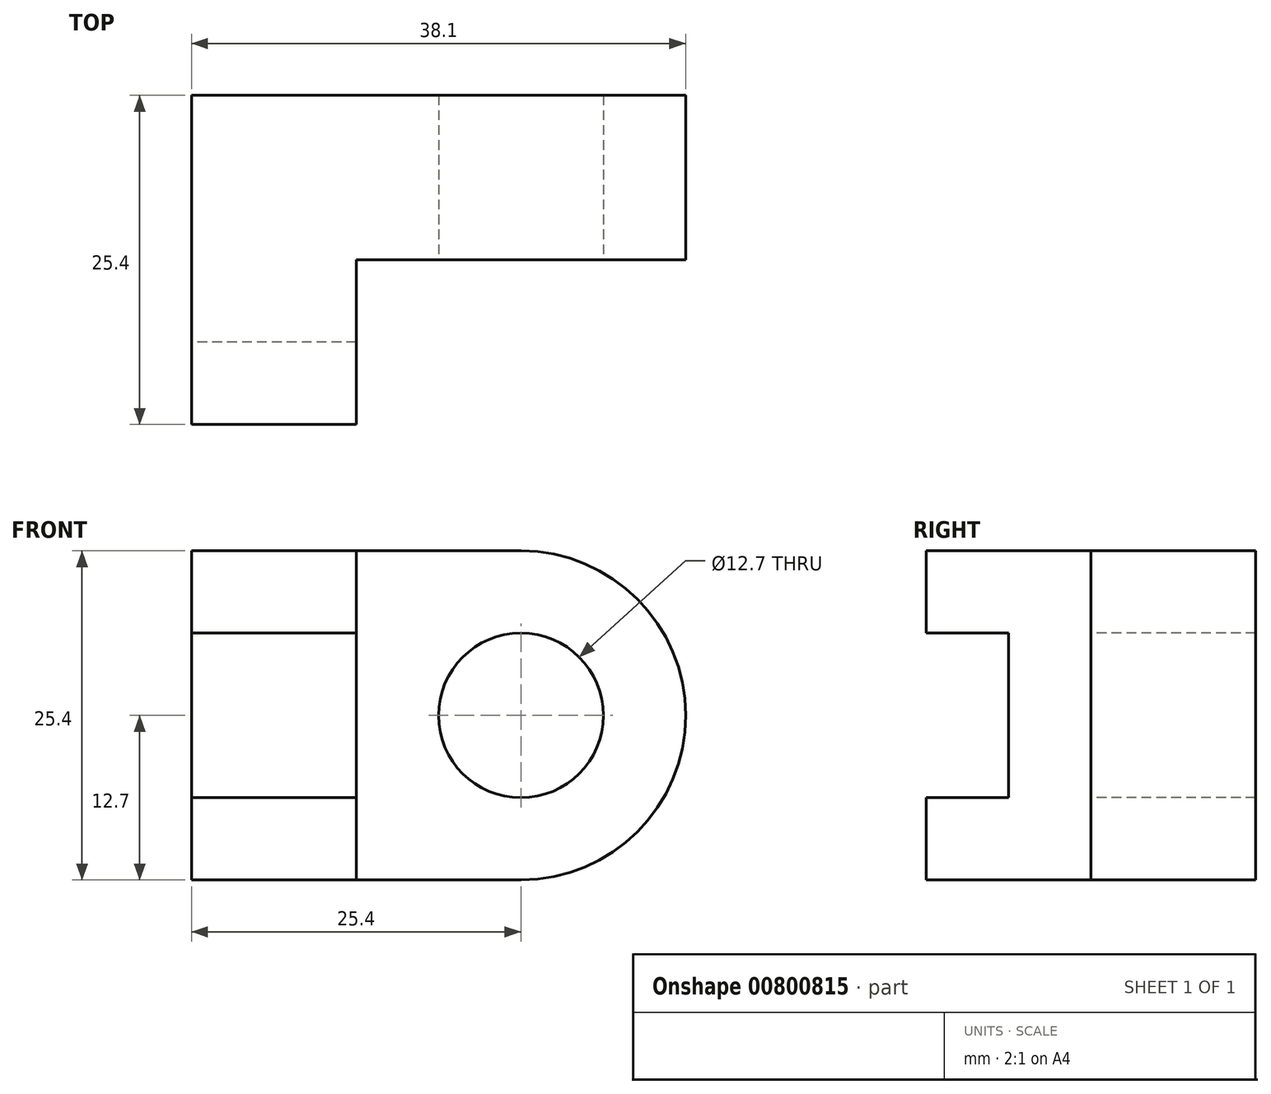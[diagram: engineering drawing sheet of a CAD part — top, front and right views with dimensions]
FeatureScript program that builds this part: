
annotation { "Feature Type Name" : "Feature", "Feature Type Description" : "" }
export const myFeature = defineFeature(function(context is Context, id is Id, definition is map)
    precondition{}
    {
        {
            var Q0;
            Q0=qCreatedBy(makeId("Front.planeOp"),FACE);
            var sketch = newSketch(context, id + "F0", { "sketchPlane" : qUnion([Q0])});
            skLineSegment(sketch, "E0", {"start": v(0, 0) * mm, "end": v(38.1, 0) * mm});
            skLineSegment(sketch, "E1", {"start": v(38.1, 0) * mm, "end": v(38.1, 25.4) * mm});
            skLineSegment(sketch, "E2", {"start": v(38.1, 25.4) * mm, "end": v(0, 25.4) * mm});
            skLineSegment(sketch, "E3", {"start": v(0, 25.4) * mm, "end": v(0, 0) * mm});
            skSolve(sketch);
        }
        {
            var Q0;
            Q0=makeQuery(id+"F0.imprint","IMPRINT",FACE,{"disambiguationData":[TD([[makeQuery(id+"F0.imprint","IMPRINT",EDGE,{"derivedFrom":sQuery(id+"F0.wireOp",EDGE,"E0")}),1.0]])]});
            extrude(context, id + "F1", {"entities" : qUnion([Q0]), "depth" : 25.4 * mm, "offsetDistance" : 25.4 * mm});
        }
        {
            var Q0;
            Q0=makeQuery(id+"F1.opExtrude","CAP_FACE",FACE,{"disambiguationData":[OSD([sQuery(id+"F0.wireOp",EDGE,"E0"),sQuery(id+"F0.wireOp",EDGE,"E1"),sQuery(id+"F0.wireOp",EDGE,"E2"),sQuery(id+"F0.wireOp",EDGE,"E3")])],"isStart":false});
            var sketch = newSketch(context, id + "F2", { "sketchPlane" : qUnion([Q0])});
            skLineSegment(sketch, "E4", {"start": v(0, 25.4) * mm, "end": v(12.7, 25.4) * mm, "construction": true});
            skLineSegment(sketch, "E5", {"start": v(12.7, 25.4) * mm, "end": v(12.7, 0) * mm});
            skSolve(sketch);
        }
        {
            var Q0;
            Q0 = qSketchRegion(id + "F2", true);
            var Q1;
            {var subQ0=sQuery(id+"F2.wireOp",EDGE,"E5");Q1=makeQuery(id+"F2.imprint","IMPRINT",FACE,{"disambiguationData":[TD([[makeQuery(id+"F2.imprint","IMPRINT",EDGE,{"derivedFrom":subQ0}),1.0]])]});}
            extrude(context, id + "F3", {"entities" : qUnion([Q0, Q1]), "operationType" : NewBodyOperationType.REMOVE, "oppositeDirection" : true, "depth" : 12.7 * mm, "offsetDistance" : 25.4 * mm});
        }
        {
            var Q0;
            Q0=makeQuery(id+"F1.opExtrude","CAP_FACE",FACE,{"disambiguationData":[OSD([sQuery(id+"F0.wireOp",EDGE,"E0"),sQuery(id+"F0.wireOp",EDGE,"E1"),sQuery(id+"F0.wireOp",EDGE,"E2"),sQuery(id+"F0.wireOp",EDGE,"E3")])],"isStart":false});
            var sketch = newSketch(context, id + "F4", { "sketchPlane" : qUnion([Q0])});
            skLineSegment(sketch, "E6", {"start": v(12.7, 25.4) * mm, "end": v(12.7, 19.05) * mm, "construction": true});
            skLineSegment(sketch, "E7", {"start": v(12.7, 19.05) * mm, "end": v(12.7, 10.85) * mm, "construction": true});
            skLineSegment(sketch, "E8", {"start": v(12.7, 19.05) * mm, "end": v(0, 19.05) * mm});
            skLineSegment(sketch, "E9", {"start": v(12.7, 19.05) * mm, "end": v(12.7, 6.35) * mm, "construction": true});
            skLineSegment(sketch, "E10", {"start": v(12.7, 6.35) * mm, "end": v(0, 6.35) * mm});
            skSolve(sketch);
        }
        {
            var Q0;
            Q0 = qSketchRegion(id + "F4", true);
            var Q1;
            {var subQ0=sQuery(id+"F4.wireOp",EDGE,"E8");Q1=makeQuery(id+"F4.imprint","IMPRINT",FACE,{"disambiguationData":[TD([[makeQuery(id+"F4.imprint","IMPRINT",EDGE,{"derivedFrom":subQ0}),1.0]])]});}
            extrude(context, id + "F5", {"entities" : qUnion([Q0, Q1]), "operationType" : NewBodyOperationType.REMOVE, "oppositeDirection" : true, "depth" : 6.35 * mm, "offsetDistance" : 25.4 * mm});
        }
        {
            var Q0;
            Q0=makeQuery(id+"F3.boolean.opBoolean","COPY",FACE,{"derivedFrom":makeQuery(id+"F3.opExtrude","CAP_FACE",FACE,{"disambiguationData":[OSD([sQuery(id+"F0.wireOp",EDGE,"E0"),sQuery(id+"F0.wireOp",EDGE,"E1"),sQuery(id+"F0.wireOp",EDGE,"E2"),sQuery(id+"F2.wireOp",EDGE,"E5")])],"isStart":false})});
            var sketch = newSketch(context, id + "F6", { "sketchPlane" : qUnion([Q0])});
            skArc(sketch, "E11", {"start": v(25.4, 0) * mm, "mid": v(38.1, 12.7) * mm, "end": v(25.4, 25.4) * mm});
            skCircle(sketch, "E12", {"center": v(25.4, 12.7) * mm, "radius": 6.35 * mm});
            skSolve(sketch);
        }
        {
            var Q0;
            Q0=makeQuery(id+"F6.imprint","IMPRINT",FACE,{"disambiguationData":[TD([[makeQuery(id+"F6.imprint","IMPRINT",EDGE,{"derivedFrom":sQuery(id+"F6.wireOp",EDGE,"E12")}),1.0]])]});
            var Q1;
            {var subQ0=sQuery(id+"F6.wireOp",EDGE,"E11");var subQ1=makeQuery(id+"F3.boolean.opBoolean","COPY",EDGE,{"derivedFrom":makeQuery(id+"F3.opExtrude","CAP_EDGE",EDGE,{"disambiguationData":[OSD([sQuery(id+"F0.wireOp",EDGE,"E2")])],"isStart":false})});var subQ2=makeQuery(id+"F6.imprint","INTERSECT",VERTEX,{"derivedFrom":[subQ1,subQ0]});Q1=makeQuery(id+"F6.imprint","IMPRINT",FACE,{"disambiguationData":[TD([[makeQuery(id+"F6.imprint","IMPRINT",EDGE,{"disambiguationData":[TD([[subQ2,1.0]])],"derivedFrom":subQ0}),-1.0]])]});}
            var Q2;
            {var subQ0=sQuery(id+"F6.wireOp",EDGE,"E11");var subQ1=makeQuery(id+"F3.boolean.opBoolean","COPY",EDGE,{"derivedFrom":makeQuery(id+"F3.opExtrude","CAP_EDGE",EDGE,{"disambiguationData":[OSD([sQuery(id+"F0.wireOp",EDGE,"E0")])],"isStart":false})});var subQ2=makeQuery(id+"F6.imprint","INTERSECT",VERTEX,{"derivedFrom":[subQ1,subQ0]});Q2=makeQuery(id+"F6.imprint","IMPRINT",FACE,{"disambiguationData":[TD([[makeQuery(id+"F6.imprint","IMPRINT",EDGE,{"disambiguationData":[TD([[subQ2,-1.0]])],"derivedFrom":subQ0}),-1.0]])]});}
            extrude(context, id + "F7", {"entities" : qUnion([Q0, Q1, Q2]), "operationType" : NewBodyOperationType.REMOVE, "endBound" : BoundingType.UP_TO_NEXT, "oppositeDirection" : true, "depth" : 25.4 * mm, "offsetDistance" : 25.4 * mm});
        }
    });
